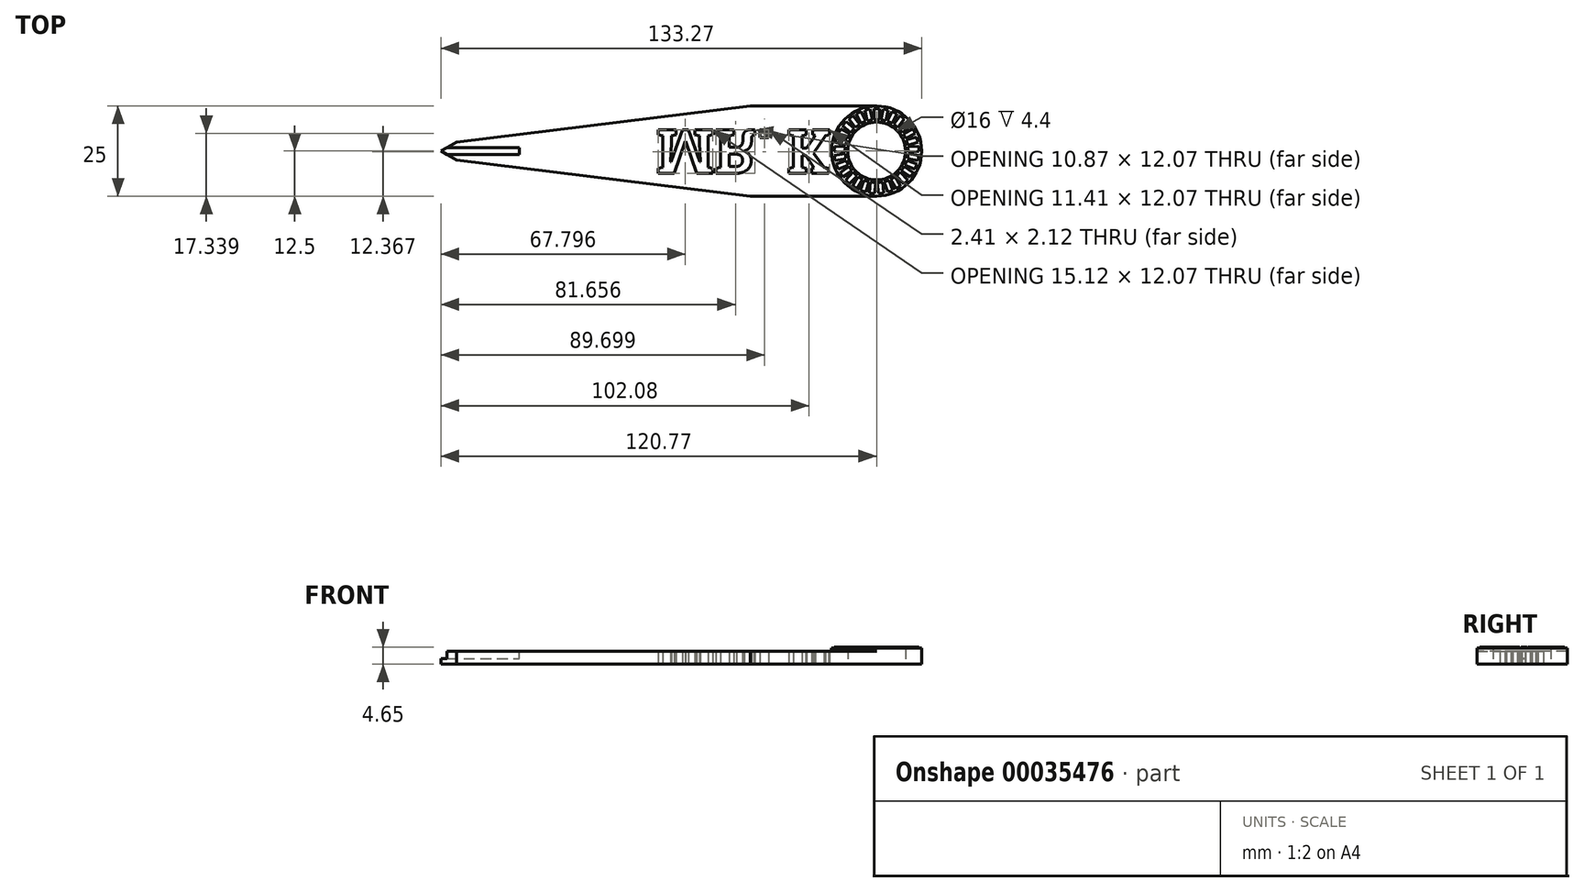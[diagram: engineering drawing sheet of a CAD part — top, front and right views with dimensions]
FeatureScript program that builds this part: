
annotation { "Feature Type Name" : "Feature", "Feature Type Description" : "" }
export const myFeature = defineFeature(function(context is Context, id is Id, definition is map)
    precondition{}
    {
        {
            var Q0;
            Q0=qCreatedBy(makeId("Top.planeOp"),FACE);
            var sketch = newSketch(context, id + "F0", { "sketchPlane" : qUnion([Q0])});
            skCircle(sketch, "E0", {"center": v(0, 0) * mm, "radius": 8 * mm});
            skCircle(sketch, "E1", {"center": v(0, 0) * mm, "radius": 12.5 * mm});
            skLineSegment(sketch, "E2", {"start": v(-35, 12.5) * mm, "end": v(0, 12.5) * mm});
            skLineSegment(sketch, "E3", {"start": v(-35, -12.5) * mm, "end": v(0, -12.5) * mm});
            skLineSegment(sketch, "E4", {"start": v(-35, 12.5) * mm, "end": v(-122.63, 12.5) * mm, "construction": true});
            skLineSegment(sketch, "E5", {"start": v(-35, 12.5) * mm, "end": v(-116.39, 2.5) * mm});
            skLineSegment(sketch, "E6", {"start": v(-35, -12.5) * mm, "end": v(-124.23, -12.5) * mm, "construction": true});
            skLineSegment(sketch, "E7", {"start": v(-35, -12.5) * mm, "end": v(-116.39, -2.5) * mm});
            skLineSegment(sketch, "E8", {"start": v(-116.39, 2.5) * mm, "end": v(-116.39, -2.5) * mm});
            skLineSegment(sketch, "E9", {"start": v(-120.77, 0) * mm, "end": v(-116.39, 2.5) * mm});
            skLineSegment(sketch, "E10", {"start": v(-120.77, 0) * mm, "end": v(-116.39, -2.5) * mm});
            skSolve(sketch);
        }
        {
            var Q0;
            Q0 = qSketchRegion(id + "F0", true);
            extrude(context, id + "F1", {"entities" : qUnion([Q0]), "depth" : 3.5 * mm});
        }
        {
            var Q0;
            Q0=qCreatedBy(makeId("Top.planeOp"),FACE);
            var sketch = newSketch(context, id + "F2", { "sketchPlane" : qUnion([Q0])});
            skCircle(sketch, "E11", {"center": v(0, 0) * mm, "radius": 8 * mm});
            skCircle(sketch, "E12", {"center": v(0, 0) * mm, "radius": 12.5 * mm});
            skSolve(sketch);
        }
        {
            var Q0;
            Q0 = qSketchRegion(id + "FTT6pSvakFv8IsX_1", true);
            var Q1;
            Q1 = qSketchRegion(id + "F2", true);
            extrude(context, id + "F3", {"entities" : qUnion([Q0, Q1]), "operationType" : NewBodyOperationType.ADD, "depth" : 4.4 * mm});
        }
        {
            var Q0;
            Q0=makeQuery(id+"F1.opExtrude","CAP_FACE",FACE,{"disambiguationData":[OSD([sQuery(id+"F0.wireOp",EDGE,"E0"),sQuery(id+"F0.wireOp",EDGE,"E1"),sQuery(id+"F0.wireOp",EDGE,"E2"),sQuery(id+"F0.wireOp",EDGE,"E3"),sQuery(id+"F0.wireOp",EDGE,"E5"),sQuery(id+"F0.wireOp",EDGE,"E7"),sQuery(id+"F0.wireOp",EDGE,"E9"),sQuery(id+"F0.wireOp",EDGE,"E10"),sQuery(id+"F0.wireOp",EDGE,"41b71ed3-3365-47f3-8b95-72667886b5d8.sketch_text.stroke-0"),sQuery(id+"F0.wireOp",EDGE,"41b71ed3-3365-47f3-8b95-72667886b5d8.sketch_text.stroke-1"),sQuery(id+"F0.wireOp",EDGE,"41b71ed3-3365-47f3-8b95-72667886b5d8.sketch_text.stroke-2"),sQuery(id+"F0.wireOp",EDGE,"41b71ed3-3365-47f3-8b95-72667886b5d8.sketch_text.stroke-3"),sQuery(id+"F0.wireOp",EDGE,"41b71ed3-3365-47f3-8b95-72667886b5d8.sketch_text.stroke-4"),sQuery(id+"F0.wireOp",EDGE,"41b71ed3-3365-47f3-8b95-72667886b5d8.sketch_text.stroke-5"),sQuery(id+"F0.wireOp",EDGE,"41b71ed3-3365-47f3-8b95-72667886b5d8.sketch_text.stroke-6"),sQuery(id+"F0.wireOp",EDGE,"41b71ed3-3365-47f3-8b95-72667886b5d8.sketch_text.stroke-7"),sQuery(id+"F0.wireOp",EDGE,"41b71ed3-3365-47f3-8b95-72667886b5d8.sketch_text.stroke-8"),sQuery(id+"F0.wireOp",EDGE,"41b71ed3-3365-47f3-8b95-72667886b5d8.sketch_text.stroke-9"),sQuery(id+"F0.wireOp",EDGE,"41b71ed3-3365-47f3-8b95-72667886b5d8.sketch_text.stroke-10"),sQuery(id+"F0.wireOp",EDGE,"41b71ed3-3365-47f3-8b95-72667886b5d8.sketch_text.stroke-11"),sQuery(id+"F0.wireOp",EDGE,"41b71ed3-3365-47f3-8b95-72667886b5d8.sketch_text.stroke-12"),sQuery(id+"F0.wireOp",EDGE,"41b71ed3-3365-47f3-8b95-72667886b5d8.sketch_text.stroke-13"),sQuery(id+"F0.wireOp",EDGE,"41b71ed3-3365-47f3-8b95-72667886b5d8.sketch_text.stroke-14"),sQuery(id+"F0.wireOp",EDGE,"41b71ed3-3365-47f3-8b95-72667886b5d8.sketch_text.stroke-15"),sQuery(id+"F0.wireOp",EDGE,"41b71ed3-3365-47f3-8b95-72667886b5d8.sketch_text.stroke-16"),sQuery(id+"F0.wireOp",EDGE,"41b71ed3-3365-47f3-8b95-72667886b5d8.sketch_text.stroke-17"),sQuery(id+"F0.wireOp",EDGE,"41b71ed3-3365-47f3-8b95-72667886b5d8.sketch_text.stroke-18"),sQuery(id+"F0.wireOp",EDGE,"41b71ed3-3365-47f3-8b95-72667886b5d8.sketch_text.stroke-19"),sQuery(id+"F0.wireOp",EDGE,"41b71ed3-3365-47f3-8b95-72667886b5d8.sketch_text.stroke-20"),sQuery(id+"F0.wireOp",EDGE,"41b71ed3-3365-47f3-8b95-72667886b5d8.sketch_text.stroke-21"),sQuery(id+"F0.wireOp",EDGE,"41b71ed3-3365-47f3-8b95-72667886b5d8.sketch_text.stroke-22"),sQuery(id+"F0.wireOp",EDGE,"41b71ed3-3365-47f3-8b95-72667886b5d8.sketch_text.stroke-23"),sQuery(id+"F0.wireOp",EDGE,"41b71ed3-3365-47f3-8b95-72667886b5d8.sketch_text.stroke-24"),sQuery(id+"F0.wireOp",EDGE,"41b71ed3-3365-47f3-8b95-72667886b5d8.sketch_text.stroke-25"),sQuery(id+"F0.wireOp",EDGE,"41b71ed3-3365-47f3-8b95-72667886b5d8.sketch_text.stroke-26"),sQuery(id+"F0.wireOp",EDGE,"41b71ed3-3365-47f3-8b95-72667886b5d8.sketch_text.stroke-27"),sQuery(id+"F0.wireOp",EDGE,"41b71ed3-3365-47f3-8b95-72667886b5d8.sketch_text.stroke-28"),sQuery(id+"F0.wireOp",EDGE,"41b71ed3-3365-47f3-8b95-72667886b5d8.sketch_text.stroke-29"),sQuery(id+"F0.wireOp",EDGE,"41b71ed3-3365-47f3-8b95-72667886b5d8.sketch_text.stroke-30"),sQuery(id+"F0.wireOp",EDGE,"41b71ed3-3365-47f3-8b95-72667886b5d8.sketch_text.stroke-31"),sQuery(id+"F0.wireOp",EDGE,"41b71ed3-3365-47f3-8b95-72667886b5d8.sketch_text.stroke-32"),sQuery(id+"F0.wireOp",EDGE,"41b71ed3-3365-47f3-8b95-72667886b5d8.sketch_text.stroke-33"),sQuery(id+"F0.wireOp",EDGE,"41b71ed3-3365-47f3-8b95-72667886b5d8.sketch_text.stroke-34"),sQuery(id+"F0.wireOp",EDGE,"41b71ed3-3365-47f3-8b95-72667886b5d8.sketch_text.stroke-35"),sQuery(id+"F0.wireOp",EDGE,"41b71ed3-3365-47f3-8b95-72667886b5d8.sketch_text.stroke-36"),sQuery(id+"F0.wireOp",EDGE,"41b71ed3-3365-47f3-8b95-72667886b5d8.sketch_text.stroke-37"),sQuery(id+"F0.wireOp",EDGE,"41b71ed3-3365-47f3-8b95-72667886b5d8.sketch_text.stroke-38"),sQuery(id+"F0.wireOp",EDGE,"41b71ed3-3365-47f3-8b95-72667886b5d8.sketch_text.stroke-39"),sQuery(id+"F0.wireOp",EDGE,"41b71ed3-3365-47f3-8b95-72667886b5d8.sketch_text.stroke-40"),sQuery(id+"F0.wireOp",EDGE,"41b71ed3-3365-47f3-8b95-72667886b5d8.sketch_text.stroke-41"),sQuery(id+"F0.wireOp",EDGE,"41b71ed3-3365-47f3-8b95-72667886b5d8.sketch_text.stroke-42"),sQuery(id+"F0.wireOp",EDGE,"41b71ed3-3365-47f3-8b95-72667886b5d8.sketch_text.stroke-43"),sQuery(id+"F0.wireOp",EDGE,"41b71ed3-3365-47f3-8b95-72667886b5d8.sketch_text.stroke-44"),sQuery(id+"F0.wireOp",EDGE,"41b71ed3-3365-47f3-8b95-72667886b5d8.sketch_text.stroke-45"),sQuery(id+"F0.wireOp",EDGE,"41b71ed3-3365-47f3-8b95-72667886b5d8.sketch_text.stroke-46"),sQuery(id+"F0.wireOp",EDGE,"41b71ed3-3365-47f3-8b95-72667886b5d8.sketch_text.stroke-47"),sQuery(id+"F0.wireOp",EDGE,"41b71ed3-3365-47f3-8b95-72667886b5d8.sketch_text.stroke-48"),sQuery(id+"F0.wireOp",EDGE,"41b71ed3-3365-47f3-8b95-72667886b5d8.sketch_text.stroke-49"),sQuery(id+"F0.wireOp",EDGE,"41b71ed3-3365-47f3-8b95-72667886b5d8.sketch_text.stroke-50"),sQuery(id+"F0.wireOp",EDGE,"41b71ed3-3365-47f3-8b95-72667886b5d8.sketch_text.stroke-51"),sQuery(id+"F0.wireOp",EDGE,"41b71ed3-3365-47f3-8b95-72667886b5d8.sketch_text.stroke-52"),sQuery(id+"F0.wireOp",EDGE,"41b71ed3-3365-47f3-8b95-72667886b5d8.sketch_text.stroke-53"),sQuery(id+"F0.wireOp",EDGE,"41b71ed3-3365-47f3-8b95-72667886b5d8.sketch_text.stroke-54"),sQuery(id+"F0.wireOp",EDGE,"41b71ed3-3365-47f3-8b95-72667886b5d8.sketch_text.stroke-55"),sQuery(id+"F0.wireOp",EDGE,"41b71ed3-3365-47f3-8b95-72667886b5d8.sketch_text.stroke-56"),sQuery(id+"F0.wireOp",EDGE,"41b71ed3-3365-47f3-8b95-72667886b5d8.sketch_text.stroke-57"),sQuery(id+"F0.wireOp",EDGE,"41b71ed3-3365-47f3-8b95-72667886b5d8.sketch_text.stroke-58"),sQuery(id+"F0.wireOp",EDGE,"41b71ed3-3365-47f3-8b95-72667886b5d8.sketch_text.stroke-59"),sQuery(id+"F0.wireOp",EDGE,"41b71ed3-3365-47f3-8b95-72667886b5d8.sketch_text.stroke-67"),sQuery(id+"F0.wireOp",EDGE,"41b71ed3-3365-47f3-8b95-72667886b5d8.sketch_text.stroke-68"),sQuery(id+"F0.wireOp",EDGE,"41b71ed3-3365-47f3-8b95-72667886b5d8.sketch_text.stroke-69"),sQuery(id+"F0.wireOp",EDGE,"41b71ed3-3365-47f3-8b95-72667886b5d8.sketch_text.stroke-70"),sQuery(id+"F0.wireOp",EDGE,"41b71ed3-3365-47f3-8b95-72667886b5d8.sketch_text.stroke-71"),sQuery(id+"F0.wireOp",EDGE,"41b71ed3-3365-47f3-8b95-72667886b5d8.sketch_text.stroke-72"),sQuery(id+"F0.wireOp",EDGE,"41b71ed3-3365-47f3-8b95-72667886b5d8.sketch_text.stroke-73"),sQuery(id+"F0.wireOp",EDGE,"41b71ed3-3365-47f3-8b95-72667886b5d8.sketch_text.stroke-74"),sQuery(id+"F0.wireOp",EDGE,"41b71ed3-3365-47f3-8b95-72667886b5d8.sketch_text.stroke-75"),sQuery(id+"F0.wireOp",EDGE,"41b71ed3-3365-47f3-8b95-72667886b5d8.sketch_text.stroke-76"),sQuery(id+"F0.wireOp",EDGE,"41b71ed3-3365-47f3-8b95-72667886b5d8.sketch_text.stroke-77"),sQuery(id+"F0.wireOp",EDGE,"41b71ed3-3365-47f3-8b95-72667886b5d8.sketch_text.stroke-78"),sQuery(id+"F0.wireOp",EDGE,"41b71ed3-3365-47f3-8b95-72667886b5d8.sketch_text.stroke-79"),sQuery(id+"F0.wireOp",EDGE,"41b71ed3-3365-47f3-8b95-72667886b5d8.sketch_text.stroke-80"),sQuery(id+"F0.wireOp",EDGE,"41b71ed3-3365-47f3-8b95-72667886b5d8.sketch_text.stroke-81"),sQuery(id+"F0.wireOp",EDGE,"41b71ed3-3365-47f3-8b95-72667886b5d8.sketch_text.stroke-82"),sQuery(id+"F0.wireOp",EDGE,"41b71ed3-3365-47f3-8b95-72667886b5d8.sketch_text.stroke-83"),sQuery(id+"F0.wireOp",EDGE,"41b71ed3-3365-47f3-8b95-72667886b5d8.sketch_text.stroke-84"),sQuery(id+"F0.wireOp",EDGE,"41b71ed3-3365-47f3-8b95-72667886b5d8.sketch_text.stroke-85"),sQuery(id+"F0.wireOp",EDGE,"41b71ed3-3365-47f3-8b95-72667886b5d8.sketch_text.stroke-86"),sQuery(id+"F0.wireOp",EDGE,"41b71ed3-3365-47f3-8b95-72667886b5d8.sketch_text.stroke-87"),sQuery(id+"F0.wireOp",EDGE,"41b71ed3-3365-47f3-8b95-72667886b5d8.sketch_text.stroke-88"),sQuery(id+"F0.wireOp",EDGE,"41b71ed3-3365-47f3-8b95-72667886b5d8.sketch_text.stroke-89"),sQuery(id+"F0.wireOp",EDGE,"41b71ed3-3365-47f3-8b95-72667886b5d8.sketch_text.stroke-90"),sQuery(id+"F0.wireOp",EDGE,"41b71ed3-3365-47f3-8b95-72667886b5d8.sketch_text.stroke-91"),sQuery(id+"F0.wireOp",EDGE,"41b71ed3-3365-47f3-8b95-72667886b5d8.sketch_text.stroke-92"),sQuery(id+"F0.wireOp",EDGE,"41b71ed3-3365-47f3-8b95-72667886b5d8.sketch_text.stroke-93"),sQuery(id+"F0.wireOp",EDGE,"41b71ed3-3365-47f3-8b95-72667886b5d8.sketch_text.stroke-94"),sQuery(id+"F0.wireOp",EDGE,"41b71ed3-3365-47f3-8b95-72667886b5d8.sketch_text.stroke-95"),sQuery(id+"F0.wireOp",EDGE,"41b71ed3-3365-47f3-8b95-72667886b5d8.sketch_text.stroke-96"),sQuery(id+"F0.wireOp",EDGE,"41b71ed3-3365-47f3-8b95-72667886b5d8.sketch_text.stroke-97"),sQuery(id+"F0.wireOp",EDGE,"41b71ed3-3365-47f3-8b95-72667886b5d8.sketch_text.stroke-98"),sQuery(id+"F0.wireOp",EDGE,"41b71ed3-3365-47f3-8b95-72667886b5d8.sketch_text.stroke-99")])],"isStart":false});
            var sketch = newSketch(context, id + "F4", { "sketchPlane" : qUnion([Q0])});
            skLineSegment(sketch, "E13", {"start": v(-120.77, 0) * mm, "end": v(-119.02, 1) * mm});
            skLineSegment(sketch, "E14", {"start": v(-119.02, 1) * mm, "end": v(-99.02, 1) * mm});
            skLineSegment(sketch, "E15", {"start": v(-99.02, 1) * mm, "end": v(-99.02, -1) * mm});
            skLineSegment(sketch, "E16", {"start": v(-99.02, -1) * mm, "end": v(-119.02, -1) * mm});
            skLineSegment(sketch, "E17", {"start": v(-119.02, -1) * mm, "end": v(-120.77, 0) * mm});
            skSolve(sketch);
        }
        {
            var Q0;
            Q0 = qSketchRegion(id + "F4", true);
            extrude(context, id + "F5", {"entities" : qUnion([Q0]), "operationType" : NewBodyOperationType.REMOVE, "oppositeDirection" : true, "depth" : 2 * mm});
        }
        {
            var Q0;
            Q0=makeQuery(id+"F3.opExtrude","CAP_FACE",FACE,{"disambiguationData":[OSD([sQuery(id+"F2.wireOp",EDGE,"E11"),sQuery(id+"F2.wireOp",EDGE,"E12")])],"isStart":false});
            var sketch = newSketch(context, id + "F6", { "sketchPlane" : qUnion([Q0])});
            skLineSegment(sketch, "E18.bottom", {"start": v(-0.75, 11.75) * mm, "end": v(0.75, 11.75) * mm});
            skLineSegment(sketch, "E18.top", {"start": v(-0.75, 8.75) * mm, "end": v(0.75, 8.75) * mm});
            skLineSegment(sketch, "E18.left", {"start": v(-0.75, 11.75) * mm, "end": v(-0.75, 8.75) * mm});
            skLineSegment(sketch, "E18.right", {"start": v(0.75, 11.75) * mm, "end": v(0.75, 8.75) * mm});
            skLineSegment(sketch, "E19.1.0", {"start": v(3.26, 11.31) * mm, "end": v(2.61, 8.38) * mm});
            skLineSegment(sketch, "E19.1.1", {"start": v(1.15, 8.7) * mm, "end": v(2.61, 8.38) * mm});
            skLineSegment(sketch, "E19.1.2", {"start": v(1.8, 11.64) * mm, "end": v(1.15, 8.7) * mm});
            skLineSegment(sketch, "E19.1.3", {"start": v(1.8, 11.64) * mm, "end": v(3.26, 11.31) * mm});
            skLineSegment(sketch, "E19.2.0", {"start": v(5.61, 10.35) * mm, "end": v(4.35, 7.63) * mm});
            skLineSegment(sketch, "E19.2.1", {"start": v(3, 8.26) * mm, "end": v(4.35, 7.63) * mm});
            skLineSegment(sketch, "E19.2.2", {"start": v(4.25, 10.98) * mm, "end": v(3, 8.26) * mm});
            skLineSegment(sketch, "E19.2.3", {"start": v(4.25, 10.98) * mm, "end": v(5.61, 10.35) * mm});
            skLineSegment(sketch, "E19.3.0", {"start": v(7.7, 8.9) * mm, "end": v(5.9, 6.51) * mm});
            skLineSegment(sketch, "E19.3.1", {"start": v(4.7, 7.42) * mm, "end": v(5.9, 6.51) * mm});
            skLineSegment(sketch, "E19.3.2", {"start": v(6.51, 9.8) * mm, "end": v(4.7, 7.42) * mm});
            skLineSegment(sketch, "E19.3.3", {"start": v(6.51, 9.8) * mm, "end": v(7.7, 8.9) * mm});
            skLineSegment(sketch, "E19.4.0", {"start": v(9.44, 7.04) * mm, "end": v(7.15, 5.1) * mm});
            skLineSegment(sketch, "E19.4.1", {"start": v(6.18, 6.24) * mm, "end": v(7.15, 5.1) * mm});
            skLineSegment(sketch, "E19.4.2", {"start": v(8.47, 8.18) * mm, "end": v(6.18, 6.24) * mm});
            skLineSegment(sketch, "E19.4.3", {"start": v(8.47, 8.18) * mm, "end": v(9.44, 7.04) * mm});
            skLineSegment(sketch, "E19.5.0", {"start": v(10.73, 4.84) * mm, "end": v(8.08, 3.44) * mm});
            skLineSegment(sketch, "E19.5.1", {"start": v(7.38, 4.76) * mm, "end": v(8.08, 3.44) * mm});
            skLineSegment(sketch, "E19.5.2", {"start": v(10.03, 6.17) * mm, "end": v(7.38, 4.76) * mm});
            skLineSegment(sketch, "E19.5.3", {"start": v(10.03, 6.17) * mm, "end": v(10.73, 4.84) * mm});
            skLineSegment(sketch, "E19.6.0", {"start": v(11.52, 2.42) * mm, "end": v(8.63, 1.62) * mm});
            skLineSegment(sketch, "E19.6.1", {"start": v(8.23, 3.06) * mm, "end": v(8.63, 1.62) * mm});
            skLineSegment(sketch, "E19.6.2", {"start": v(11.12, 3.87) * mm, "end": v(8.23, 3.06) * mm});
            skLineSegment(sketch, "E19.6.3", {"start": v(11.12, 3.87) * mm, "end": v(11.52, 2.42) * mm});
            skLineSegment(sketch, "E19.7.0", {"start": v(11.77, -0.11) * mm, "end": v(8.78, -0.28) * mm});
            skLineSegment(sketch, "E19.7.1", {"start": v(8.7, 1.22) * mm, "end": v(8.78, -0.28) * mm});
            skLineSegment(sketch, "E19.7.2", {"start": v(11.7, 1.39) * mm, "end": v(8.7, 1.22) * mm});
            skLineSegment(sketch, "E19.7.3", {"start": v(11.7, 1.39) * mm, "end": v(11.77, -0.11) * mm});
            skLineSegment(sketch, "E19.8.0", {"start": v(11.47, -2.64) * mm, "end": v(8.51, -2.16) * mm});
            skLineSegment(sketch, "E19.8.1", {"start": v(8.76, -0.68) * mm, "end": v(8.51, -2.16) * mm});
            skLineSegment(sketch, "E19.8.2", {"start": v(11.72, -1.16) * mm, "end": v(8.76, -0.68) * mm});
            skLineSegment(sketch, "E19.8.3", {"start": v(11.72, -1.16) * mm, "end": v(11.47, -2.64) * mm});
            skLineSegment(sketch, "E19.9.0", {"start": v(10.64, -5.05) * mm, "end": v(7.85, -3.94) * mm});
            skLineSegment(sketch, "E19.9.1", {"start": v(8.4, -2.54) * mm, "end": v(7.85, -3.94) * mm});
            skLineSegment(sketch, "E19.9.2", {"start": v(11.2, -3.65) * mm, "end": v(8.4, -2.54) * mm});
            skLineSegment(sketch, "E19.9.3", {"start": v(11.2, -3.65) * mm, "end": v(10.64, -5.05) * mm});
            skLineSegment(sketch, "E19.10.0", {"start": v(9.3, -7.21) * mm, "end": v(6.82, -5.53) * mm});
            skLineSegment(sketch, "E19.10.1", {"start": v(7.66, -4.29) * mm, "end": v(6.82, -5.53) * mm});
            skLineSegment(sketch, "E19.10.2", {"start": v(10.15, -5.97) * mm, "end": v(7.66, -4.29) * mm});
            skLineSegment(sketch, "E19.10.3", {"start": v(10.15, -5.97) * mm, "end": v(9.3, -7.21) * mm});
            skLineSegment(sketch, "E19.11.0", {"start": v(7.54, -9.05) * mm, "end": v(5.47, -6.87) * mm});
            skLineSegment(sketch, "E19.11.1", {"start": v(6.56, -5.84) * mm, "end": v(5.47, -6.87) * mm});
            skLineSegment(sketch, "E19.11.2", {"start": v(8.62, -8.01) * mm, "end": v(6.56, -5.84) * mm});
            skLineSegment(sketch, "E19.11.3", {"start": v(8.62, -8.01) * mm, "end": v(7.54, -9.05) * mm});
            skLineSegment(sketch, "E19.12.0", {"start": v(5.42, -10.45) * mm, "end": v(3.87, -7.88) * mm});
            skLineSegment(sketch, "E19.12.1", {"start": v(5.15, -7.11) * mm, "end": v(3.87, -7.88) * mm});
            skLineSegment(sketch, "E19.12.2", {"start": v(6.7, -9.68) * mm, "end": v(5.15, -7.11) * mm});
            skLineSegment(sketch, "E19.12.3", {"start": v(5.42, -10.45) * mm, "end": v(6.7, -9.68) * mm});
            skLineSegment(sketch, "E19.13.0", {"start": v(3.04, -11.37) * mm, "end": v(2.08, -8.53) * mm});
            skLineSegment(sketch, "E19.13.1", {"start": v(3.5, -8.05) * mm, "end": v(2.08, -8.53) * mm});
            skLineSegment(sketch, "E19.13.2", {"start": v(4.46, -10.9) * mm, "end": v(3.5, -8.05) * mm});
            skLineSegment(sketch, "E19.13.3", {"start": v(4.46, -10.9) * mm, "end": v(3.04, -11.37) * mm});
            skLineSegment(sketch, "E19.14.0", {"start": v(0.52, -11.76) * mm, "end": v(0.2, -8.78) * mm});
            skLineSegment(sketch, "E19.14.1", {"start": v(1.7, -8.62) * mm, "end": v(0.2, -8.78) * mm});
            skLineSegment(sketch, "E19.14.2", {"start": v(2.02, -11.6) * mm, "end": v(1.7, -8.62) * mm});
            skLineSegment(sketch, "E19.14.3", {"start": v(2.02, -11.6) * mm, "end": v(0.52, -11.76) * mm});
            skLineSegment(sketch, "E19.15.0", {"start": v(-2.02, -11.6) * mm, "end": v(-1.7, -8.62) * mm});
            skLineSegment(sketch, "E19.15.1", {"start": v(-0.2, -8.78) * mm, "end": v(-1.7, -8.62) * mm});
            skLineSegment(sketch, "E19.15.2", {"start": v(-0.52, -11.76) * mm, "end": v(-0.2, -8.78) * mm});
            skLineSegment(sketch, "E19.15.3", {"start": v(-0.52, -11.76) * mm, "end": v(-2.02, -11.6) * mm});
            skLineSegment(sketch, "E19.16.0", {"start": v(-4.46, -10.9) * mm, "end": v(-3.5, -8.05) * mm});
            skLineSegment(sketch, "E19.16.1", {"start": v(-3.5, -8.05) * mm, "end": v(-2.08, -8.53) * mm});
            skLineSegment(sketch, "E19.16.2", {"start": v(-3.04, -11.37) * mm, "end": v(-2.08, -8.53) * mm});
            skLineSegment(sketch, "E19.16.3", {"start": v(-3.04, -11.37) * mm, "end": v(-4.46, -10.9) * mm});
            skLineSegment(sketch, "E19.17.0", {"start": v(-6.7, -9.68) * mm, "end": v(-5.15, -7.11) * mm});
            skLineSegment(sketch, "E19.17.1", {"start": v(-3.87, -7.88) * mm, "end": v(-5.15, -7.11) * mm});
            skLineSegment(sketch, "E19.17.2", {"start": v(-5.42, -10.45) * mm, "end": v(-3.87, -7.88) * mm});
            skLineSegment(sketch, "E19.17.3", {"start": v(-5.42, -10.45) * mm, "end": v(-6.7, -9.68) * mm});
            skLineSegment(sketch, "E19.18.0", {"start": v(-8.62, -8.01) * mm, "end": v(-6.56, -5.84) * mm});
            skLineSegment(sketch, "E19.18.1", {"start": v(-5.47, -6.87) * mm, "end": v(-6.56, -5.84) * mm});
            skLineSegment(sketch, "E19.18.2", {"start": v(-7.54, -9.05) * mm, "end": v(-5.47, -6.87) * mm});
            skLineSegment(sketch, "E19.18.3", {"start": v(-7.54, -9.05) * mm, "end": v(-8.62, -8.01) * mm});
            skLineSegment(sketch, "E19.19.0", {"start": v(-10.15, -5.97) * mm, "end": v(-7.66, -4.29) * mm});
            skLineSegment(sketch, "E19.19.1", {"start": v(-6.82, -5.53) * mm, "end": v(-7.66, -4.29) * mm});
            skLineSegment(sketch, "E19.19.2", {"start": v(-9.3, -7.21) * mm, "end": v(-6.82, -5.53) * mm});
            skLineSegment(sketch, "E19.19.3", {"start": v(-9.3, -7.21) * mm, "end": v(-10.15, -5.97) * mm});
            skLineSegment(sketch, "E19.20.0", {"start": v(-11.2, -3.65) * mm, "end": v(-8.4, -2.54) * mm});
            skLineSegment(sketch, "E19.20.1", {"start": v(-7.85, -3.94) * mm, "end": v(-8.4, -2.54) * mm});
            skLineSegment(sketch, "E19.20.2", {"start": v(-10.64, -5.05) * mm, "end": v(-7.85, -3.94) * mm});
            skLineSegment(sketch, "E19.20.3", {"start": v(-10.64, -5.05) * mm, "end": v(-11.2, -3.65) * mm});
            skLineSegment(sketch, "E19.21.0", {"start": v(-11.72, -1.16) * mm, "end": v(-8.76, -0.68) * mm});
            skLineSegment(sketch, "E19.21.1", {"start": v(-8.51, -2.16) * mm, "end": v(-8.76, -0.68) * mm});
            skLineSegment(sketch, "E19.21.2", {"start": v(-11.47, -2.64) * mm, "end": v(-8.51, -2.16) * mm});
            skLineSegment(sketch, "E19.21.3", {"start": v(-11.47, -2.64) * mm, "end": v(-11.72, -1.16) * mm});
            skLineSegment(sketch, "E19.22.0", {"start": v(-11.7, 1.39) * mm, "end": v(-8.7, 1.22) * mm});
            skLineSegment(sketch, "E19.22.1", {"start": v(-8.78, -0.28) * mm, "end": v(-8.7, 1.22) * mm});
            skLineSegment(sketch, "E19.22.2", {"start": v(-11.77, -0.11) * mm, "end": v(-8.78, -0.28) * mm});
            skLineSegment(sketch, "E19.22.3", {"start": v(-11.77, -0.11) * mm, "end": v(-11.7, 1.39) * mm});
            skLineSegment(sketch, "E19.23.0", {"start": v(-11.12, 3.87) * mm, "end": v(-8.23, 3.06) * mm});
            skLineSegment(sketch, "E19.23.1", {"start": v(-8.63, 1.62) * mm, "end": v(-8.23, 3.06) * mm});
            skLineSegment(sketch, "E19.23.2", {"start": v(-11.52, 2.42) * mm, "end": v(-8.63, 1.62) * mm});
            skLineSegment(sketch, "E19.23.3", {"start": v(-11.52, 2.42) * mm, "end": v(-11.12, 3.87) * mm});
            skLineSegment(sketch, "E19.24.0", {"start": v(-10.03, 6.17) * mm, "end": v(-7.38, 4.76) * mm});
            skLineSegment(sketch, "E19.24.1", {"start": v(-8.08, 3.44) * mm, "end": v(-7.38, 4.76) * mm});
            skLineSegment(sketch, "E19.24.2", {"start": v(-10.73, 4.84) * mm, "end": v(-8.08, 3.44) * mm});
            skLineSegment(sketch, "E19.24.3", {"start": v(-10.73, 4.84) * mm, "end": v(-10.03, 6.17) * mm});
            skLineSegment(sketch, "E19.25.0", {"start": v(-8.47, 8.18) * mm, "end": v(-6.18, 6.24) * mm});
            skLineSegment(sketch, "E19.25.1", {"start": v(-7.15, 5.1) * mm, "end": v(-6.18, 6.24) * mm});
            skLineSegment(sketch, "E19.25.2", {"start": v(-9.44, 7.04) * mm, "end": v(-7.15, 5.1) * mm});
            skLineSegment(sketch, "E19.25.3", {"start": v(-9.44, 7.04) * mm, "end": v(-8.47, 8.18) * mm});
            skLineSegment(sketch, "E19.26.0", {"start": v(-6.51, 9.8) * mm, "end": v(-4.7, 7.42) * mm});
            skLineSegment(sketch, "E19.26.1", {"start": v(-5.9, 6.51) * mm, "end": v(-4.7, 7.42) * mm});
            skLineSegment(sketch, "E19.26.2", {"start": v(-7.7, 8.9) * mm, "end": v(-5.9, 6.51) * mm});
            skLineSegment(sketch, "E19.26.3", {"start": v(-7.7, 8.9) * mm, "end": v(-6.51, 9.8) * mm});
            skLineSegment(sketch, "E19.27.0", {"start": v(-4.25, 10.98) * mm, "end": v(-3, 8.26) * mm});
            skLineSegment(sketch, "E19.27.1", {"start": v(-4.35, 7.63) * mm, "end": v(-3, 8.26) * mm});
            skLineSegment(sketch, "E19.27.2", {"start": v(-5.61, 10.35) * mm, "end": v(-4.35, 7.63) * mm});
            skLineSegment(sketch, "E19.27.3", {"start": v(-5.61, 10.35) * mm, "end": v(-4.25, 10.98) * mm});
            skLineSegment(sketch, "E19.28.0", {"start": v(-1.8, 11.64) * mm, "end": v(-1.15, 8.7) * mm});
            skLineSegment(sketch, "E19.28.1", {"start": v(-2.61, 8.38) * mm, "end": v(-1.15, 8.7) * mm});
            skLineSegment(sketch, "E19.28.2", {"start": v(-3.26, 11.31) * mm, "end": v(-2.61, 8.38) * mm});
            skLineSegment(sketch, "E19.28.3", {"start": v(-3.26, 11.31) * mm, "end": v(-1.8, 11.64) * mm});
            skPoint(sketch, "E19.center", {"position": v(0, 0) * mm});
            skLineSegment(sketch, "E19.anchor1", {"start": v(0, 0) * mm, "end": v(0.75, 8.75) * mm, "construction": true});
            skSolve(sketch);
        }
        {
            var Q0;
            Q0 = qSketchRegion(id + "F6", true);
            extrude(context, id + "F7", {"entities" : qUnion([Q0]), "operationType" : NewBodyOperationType.ADD, "depth" : .25 * mm});
        }
        {
            var Q0;
            Q0=makeQuery(id+"F1.opExtrude","CAP_FACE",FACE,{"disambiguationData":[OSD([sQuery(id+"F0.wireOp",EDGE,"E0"),sQuery(id+"F0.wireOp",EDGE,"E1"),sQuery(id+"F0.wireOp",EDGE,"E2"),sQuery(id+"F0.wireOp",EDGE,"E3"),sQuery(id+"F0.wireOp",EDGE,"E5"),sQuery(id+"F0.wireOp",EDGE,"E7"),sQuery(id+"F0.wireOp",EDGE,"E9"),sQuery(id+"F0.wireOp",EDGE,"E10")])],"isStart":true});
            var sketch = newSketch(context, id + "F8", { "sketchPlane" : qUnion([Q0])});
            skText(sketch, "E20", { "text": "MR. K", "fontName": "RobotoSlab-Bold.ttf"});
            const initialGuessF8  = {"E20": [-0.061, -0.0059, 1, 0, 0.01222]};
            skSetInitialGuess(sketch, initialGuessF8);
            skSolve(sketch);
        }
        {
            var Q0;
            Q0 = qSketchRegion(id + "F8", true);
            extrude(context, id + "F9", {"entities" : qUnion([Q0]), "operationType" : NewBodyOperationType.REMOVE, "endBound" : BoundingType.THROUGH_ALL, "oppositeDirection" : true, "depth" : 25 * mm});
        }
    });
